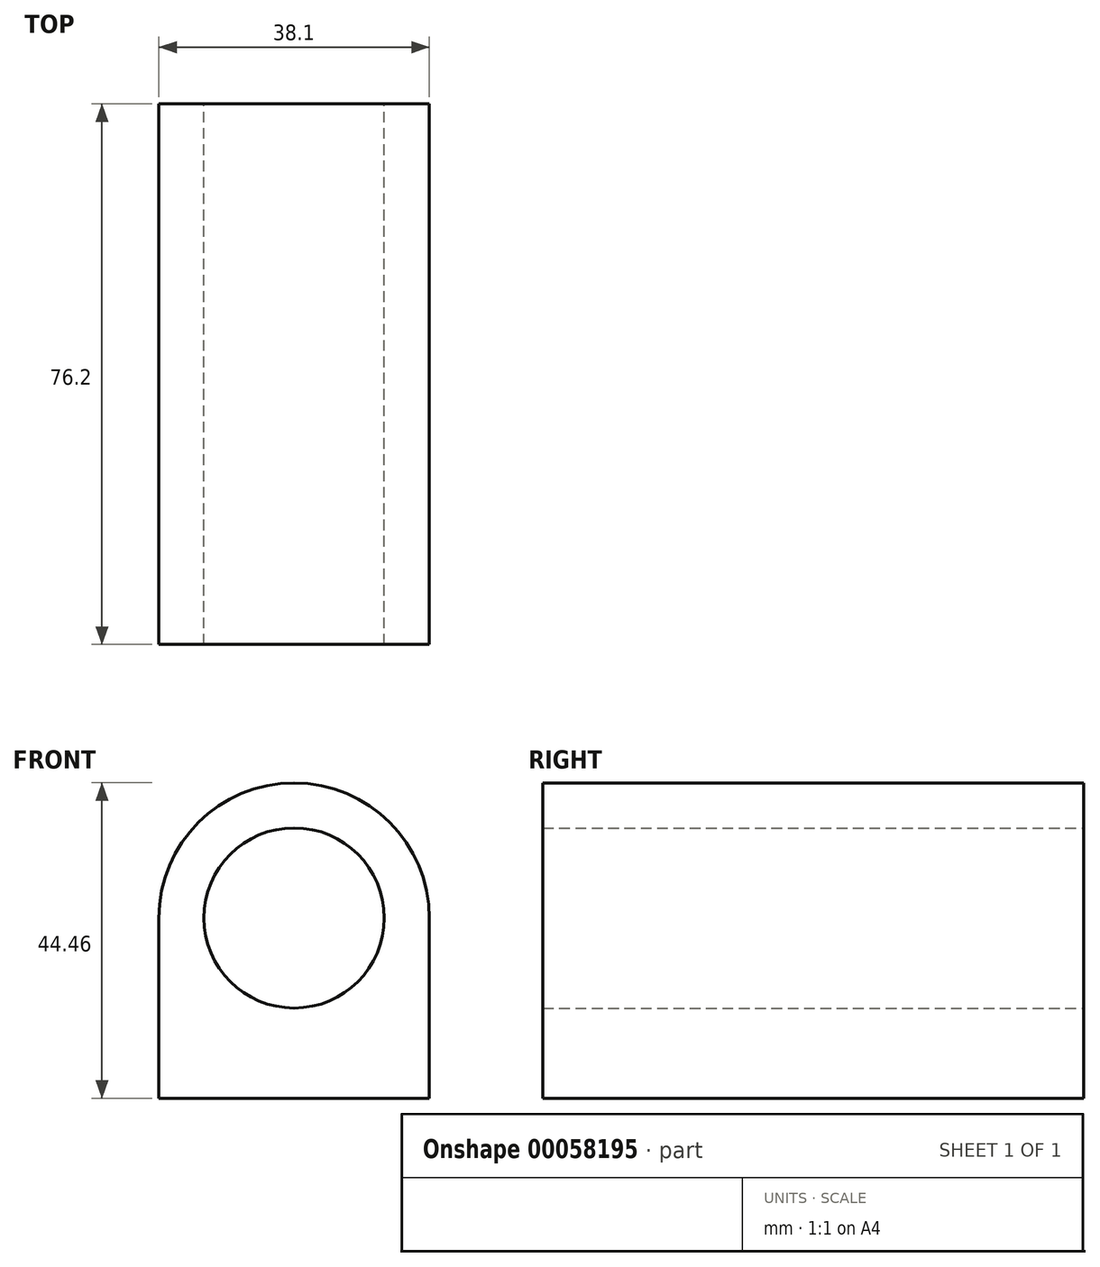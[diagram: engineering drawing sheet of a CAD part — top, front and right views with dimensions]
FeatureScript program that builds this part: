
annotation { "Feature Type Name" : "Feature", "Feature Type Description" : "" }
export const myFeature = defineFeature(function(context is Context, id is Id, definition is map)
    precondition{}
    {
        {
            var Q0;
            Q0=qCreatedBy(makeId("Front.planeOp"),FACE);
            var sketch = newSketch(context, id + "F0", { "sketchPlane" : qUnion([Q0])});
            skLineSegment(sketch, "E0.top", {"start": v(-19.05, -22.23) * mm, "end": v(19.05, -22.23) * mm});
            skLineSegment(sketch, "E0.left", {"start": v(-19.05, 3.18) * mm, "end": v(-19.05, -22.23) * mm});
            skLineSegment(sketch, "E0.right", {"start": v(19.05, 3.18) * mm, "end": v(19.05, -22.23) * mm});
            skCircle(sketch, "E1", {"center": v(0, 3.18) * mm, "radius": 19.05 * mm});
            skPoint(sketch, "E2.orphan", {"position": v(19.05, 22.23) * mm});
            skPoint(sketch, "E0.bottom.start.orphan", {"position": v(-19.05, 22.23) * mm});
            skSolve(sketch);
        }
        {
            var Q0;
            {var subQ0=sQuery(id+"F0.wireOp",EDGE,"E1");var subQ1=makeQuery(id+"F0.imprint","INTERSECT",VERTEX,{"derivedFrom":[sQuery(id+"F0.wireOp",EDGE,"E0.left"),subQ0]});Q0=makeQuery(id+"F0.imprint","IMPRINT",FACE,{"disambiguationData":[TD([[makeQuery(id+"F0.imprint","IMPRINT",EDGE,{"disambiguationData":[TD([[subQ1,1.0]])],"derivedFrom":subQ0}),1.0]])]});}
            var sketch = newSketch(context, id + "F1", { "sketchPlane" : qUnion([Q0])});
            skCircle(sketch, "E3", {"center": v(0, 3.17) * mm, "radius": 12.7 * mm});
            skSolve(sketch);
        }
        {
            var Q0;
            Q0 = qSketchRegion(id + "F1", true);
            var Q1;
            Q1 = qSketchRegion(id + "F0", true);
            extrude(context, id + "F2", {"entities" : qUnion([Q0, Q1]), "depth" : 76.2 * mm});
        }
        {
            var Q0;
            Q0 = qSketchRegion(id + "F1", true);
            extrude(context, id + "F3", {"entities" : qUnion([Q0]), "operationType" : NewBodyOperationType.REMOVE, "depth" : 76.2 * mm});
        }
    });
